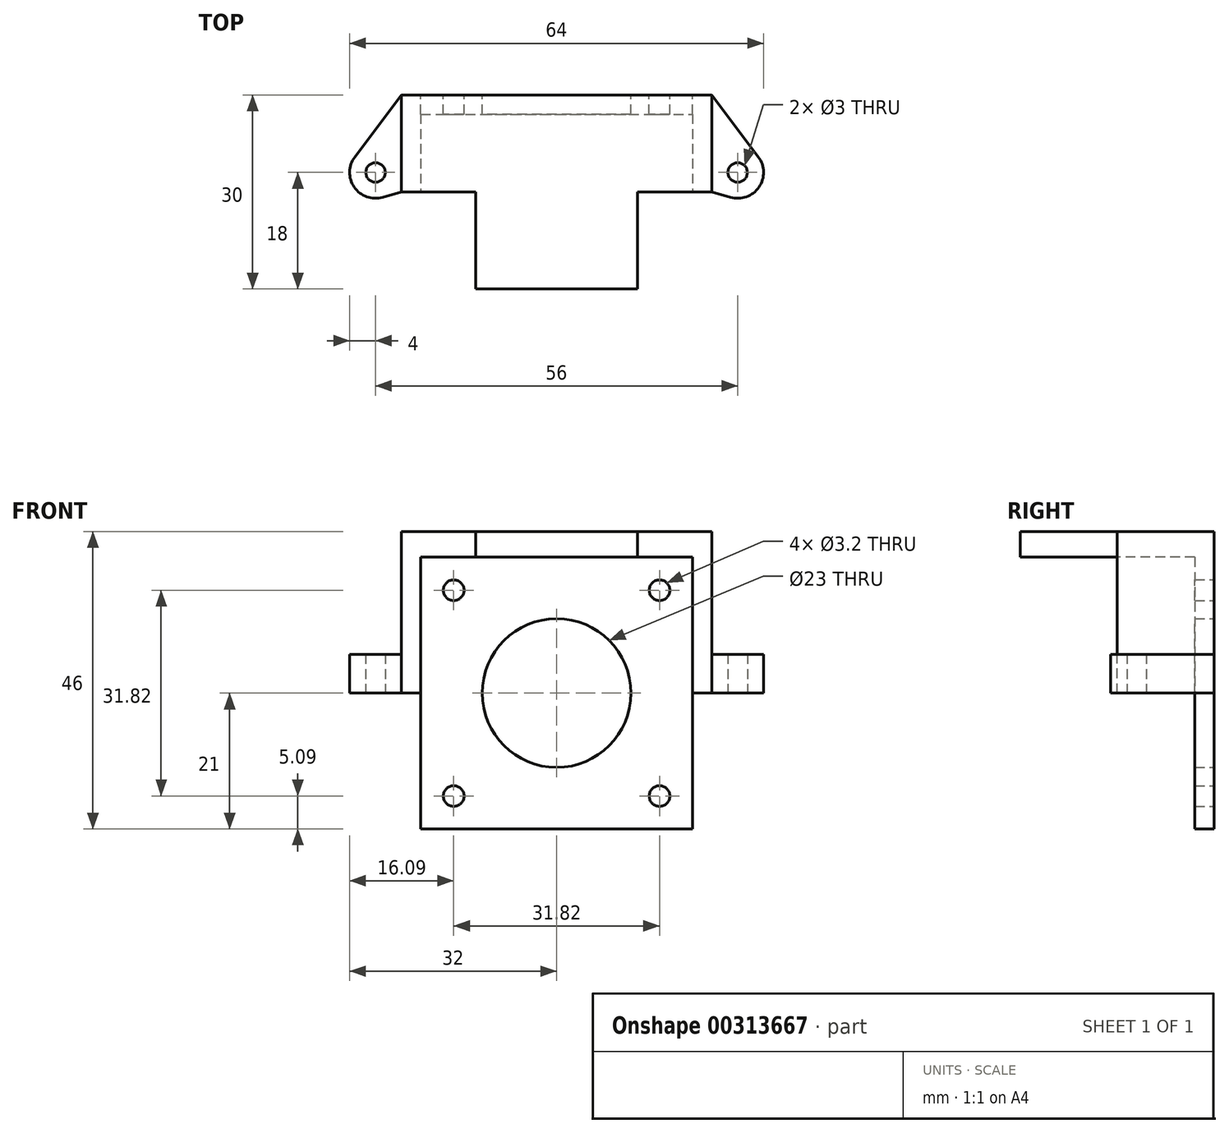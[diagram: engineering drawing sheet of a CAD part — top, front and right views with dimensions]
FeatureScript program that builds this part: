
annotation { "Feature Type Name" : "Feature", "Feature Type Description" : "" }
export const myFeature = defineFeature(function(context is Context, id is Id, definition is map)
    precondition{}
    {
        {
            var Q0;
            Q0=qCreatedBy(makeId("Front.planeOp"),FACE);
            var sketch = newSketch(context, id + "F0", { "sketchPlane" : qUnion([Q0])});
            skLineSegment(sketch, "E0.bottom", {"start": v(-21, 21) * mm, "end": v(21, 21) * mm});
            skLineSegment(sketch, "E0.top", {"start": v(-21, -21) * mm, "end": v(21, -21) * mm});
            skLineSegment(sketch, "E0.left", {"start": v(-21, 21) * mm, "end": v(-21, -21) * mm});
            skLineSegment(sketch, "E0.right", {"start": v(21, 21) * mm, "end": v(21, -21) * mm});
            skLineSegment(sketch, "E1", {"start": v(-21, 21) * mm, "end": v(21, -21) * mm});
            skLineSegment(sketch, "E2", {"start": v(21, 21) * mm, "end": v(-21, -21) * mm});
            skCircle(sketch, "E3", {"center": v(0, 0) * mm, "radius": 11.5 * mm});
            skCircle(sketch, "E4", {"center": v(-15.9, 15.9) * mm, "radius": 1.6 * mm});
            skCircle(sketch, "E5.1.0", {"center": v(-15.9, -15.9) * mm, "radius": 1.6 * mm});
            skCircle(sketch, "E5.2.0", {"center": v(15.9, -15.9) * mm, "radius": 1.6 * mm});
            skCircle(sketch, "E5.3.0", {"center": v(15.9, 15.9) * mm, "radius": 1.6 * mm});
            skSolve(sketch);
        }
        {
            var Q0;
            Q0 = qSketchRegion(id + "F0", true);
            extrude(context, id + "F1", {"entities" : qUnion([Q0]), "depth" : 3 * mm});
        }
        {
            var Q0;
            Q0=makeQuery(id+"F1.opExtrude","SWEPT_FACE",FACE,{"disambiguationData":[OSD([sQuery(id+"F0.wireOp",EDGE,"E0.bottom")])]});
            cPlane(context, id + "F2", {"entities" : qUnion([Q0]), "cplaneType" : CPlaneType.OFFSET, "offset" : 0 * mm, "width" : 150 * mm, "height" : 150 * mm});
        }
        {
            var Q0;
            Q0=qCreatedBy(id+"F2.planeOp",FACE);
            var sketch = newSketch(context, id + "F3", { "sketchPlane" : qUnion([Q0])});
            skLineSegment(sketch, "E6.bottom", {"start": v(-21, 0) * mm, "end": v(21, 0) * mm});
            skLineSegment(sketch, "E6.top", {"start": v(-21, -15) * mm, "end": v(-12.5, -15) * mm});
            skLineSegment(sketch, "E6.left", {"start": v(-21, 0) * mm, "end": v(-21, -15) * mm});
            skLineSegment(sketch, "E6.right", {"start": v(21, 0) * mm, "end": v(21, -15) * mm});
            skLineSegment(sketch, "E7.bottom", {"start": v(-12.5, -30) * mm, "end": v(12.5, -30) * mm});
            skLineSegment(sketch, "E7.left", {"start": v(-12.5, -30) * mm, "end": v(-12.5, -15) * mm});
            skLineSegment(sketch, "E7.right", {"start": v(12.5, -30) * mm, "end": v(12.5, -15) * mm});
            skLineSegment(sketch, "E8", {"start": v(0, 29.13) * mm, "end": v(0, -30) * mm});
            skLineSegment(sketch, "E9.trimOffspring", {"start": v(12.5, -15) * mm, "end": v(21, -15) * mm});
            skSolve(sketch);
        }
        {
            var Q0;
            Q0 = qSketchRegion(id + "F3", true);
            extrude(context, id + "F4", {"entities" : qUnion([Q0]), "operationType" : NewBodyOperationType.ADD, "depth" : 4 * mm});
        }
        {
            var Q0;
            Q0=qCreatedBy(makeId("Front.planeOp"),FACE);
            var sketch = newSketch(context, id + "F5", { "sketchPlane" : qUnion([Q0])});
            skLineSegment(sketch, "E10.bottom", {"start": v(-21, 0) * mm, "end": v(-24, 0) * mm});
            skLineSegment(sketch, "E10.top", {"start": v(-21, 25) * mm, "end": v(-24, 25) * mm});
            skLineSegment(sketch, "E10.left", {"start": v(-21, 0) * mm, "end": v(-21, 25) * mm});
            skLineSegment(sketch, "E10.right", {"start": v(-24, 0) * mm, "end": v(-24, 25) * mm});
            skLineSegment(sketch, "E11", {"start": v(0, 12.77) * mm, "end": v(0, -9.17) * mm});
            skLineSegment(sketch, "E12.MirrorCS", {"start": v(21, 0) * mm, "end": v(24, 0) * mm});
            skLineSegment(sketch, "E13.MirrorCS", {"start": v(21, 25) * mm, "end": v(24, 25) * mm});
            skLineSegment(sketch, "E14.MirrorCS", {"start": v(24, 0) * mm, "end": v(24, 25) * mm});
            skLineSegment(sketch, "E15.MirrorCS", {"start": v(21, 0) * mm, "end": v(21, 25) * mm});
            skSolve(sketch);
        }
        {
            var Q0;
            Q0=makeQuery(id+"F5.imprint","IMPRINT",FACE,{"disambiguationData":[TD([[makeQuery(id+"F5.imprint","IMPRINT",EDGE,{"derivedFrom":sQuery(id+"F5.wireOp",EDGE,"E10.bottom")}),-1.0]])]});
            var Q1;
            Q1=makeQuery(id+"F5.imprint","IMPRINT",FACE,{"disambiguationData":[TD([[makeQuery(id+"F5.imprint","IMPRINT",EDGE,{"derivedFrom":sQuery(id+"F5.wireOp",EDGE,"E12.MirrorCS")}),1.0]])]});
            extrude(context, id + "F6", {"entities" : qUnion([Q0, Q1]), "operationType" : NewBodyOperationType.ADD, "depth" : 15 * mm});
        }
        {
            var Q0;
            Q0=makeQuery(id+"F6.opExtrude","SWEPT_FACE",FACE,{"disambiguationData":[OSD([sQuery(id+"F5.wireOp",EDGE,"E12.MirrorCS")])]});
            cPlane(context, id + "F7", {"entities" : qUnion([Q0]), "cplaneType" : CPlaneType.OFFSET, "offset" : 0 * mm, "width" : 150 * mm, "height" : 150 * mm});
        }
        {
            var Q0;
            Q0=qCreatedBy(id+"F7.planeOp",FACE);
            var sketch = newSketch(context, id + "F8", { "sketchPlane" : qUnion([Q0])});
            skLineSegment(sketch, "E16", {"start": v(0, 0) * mm, "end": v(28, 0) * mm, "construction": true});
            skLineSegment(sketch, "E17", {"start": v(28, 0) * mm, "end": v(28, 12) * mm, "construction": true});
            skCircle(sketch, "E18", {"center": v(28, 12) * mm, "radius": 1.5 * mm});
            skArc(sketch, "E19", {"start": v(31.2, 9.6) * mm, "mid": v(31.29, 14.28) * mm, "end": v(26.88, 15.84) * mm});
            skLineSegment(sketch, "E20", {"start": v(24, 15) * mm, "end": v(26.88, 15.84) * mm});
            skLineSegment(sketch, "E21", {"start": v(24, 0) * mm, "end": v(31.2, 9.6) * mm});
            skLineSegment(sketch, "E22", {"start": v(24, 15) * mm, "end": v(24, 0) * mm});
            skLineSegment(sketch, "E23", {"start": v(0, -4.97) * mm, "end": v(0, 5.95) * mm, "construction": true});
            skLineSegment(sketch, "E24.MirrorCS", {"start": v(-24, 15) * mm, "end": v(-24, 0) * mm});
            skArc(sketch, "E25.MirrorCS", {"start": v(-31.2, 9.6) * mm, "mid": v(-31.29, 14.28) * mm, "end": v(-26.88, 15.84) * mm});
            skCircle(sketch, "E26.MirrorC", {"center": v(-28, 12) * mm, "radius": 1.5 * mm});
            skLineSegment(sketch, "E27.MirrorCS", {"start": v(-24, 0) * mm, "end": v(-31.2, 9.6) * mm});
            skLineSegment(sketch, "E28.MirrorCS", {"start": v(-28, 0) * mm, "end": v(-28, 12) * mm, "construction": true});
            skLineSegment(sketch, "E29.MirrorCS", {"start": v(-24, 15) * mm, "end": v(-26.88, 15.84) * mm});
            skSolve(sketch);
        }
        {
            var Q0;
            Q0=makeQuery(id+"F8.imprint","IMPRINT",FACE,{"disambiguationData":[TD([[makeQuery(id+"F8.imprint","IMPRINT",EDGE,{"derivedFrom":sQuery(id+"F8.wireOp",EDGE,"E18")}),-1.0]])]});
            var Q1;
            Q1=makeQuery(id+"F8.imprint","IMPRINT",FACE,{"disambiguationData":[TD([[makeQuery(id+"F8.imprint","IMPRINT",EDGE,{"derivedFrom":sQuery(id+"F8.wireOp",EDGE,"E24.MirrorCS")}),-1.0]])]});
            extrude(context, id + "F9", {"entities" : qUnion([Q0, Q1]), "operationType" : NewBodyOperationType.ADD, "oppositeDirection" : true, "depth" : 6 * mm});
        }
    });
